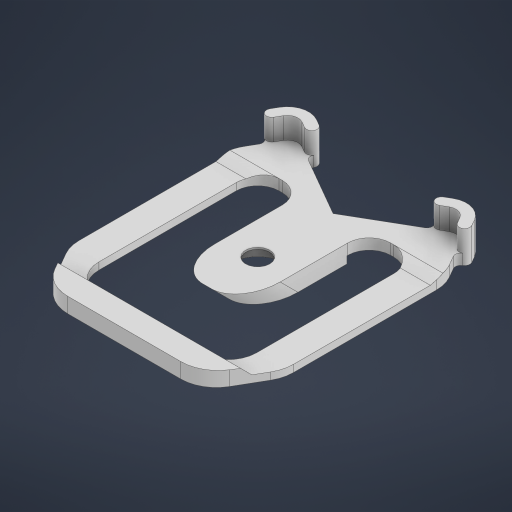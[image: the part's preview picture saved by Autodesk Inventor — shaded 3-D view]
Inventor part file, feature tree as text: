
AUTODESK INVENTOR PART (.ipt)
format: ipt  version: 2023 (Build 270158000, 158)  size: 441,344 bytes
history: native  units: in
note: dims shown in document units (in); Inventor stores cm internally (conversion verified against a paired STEP export)
features: extrude x7, chamfer x4, sketch x2, fillet x2, draft x1
ambient origin geometry x8: Origin, YZ Plane, XZ Plane, XY Plane, X Axis, Y Axis, Z Axis, Center Point
bodies: Solid1 (feature_tree)
feature tree (16):
  extrude  "Extrusion1"  Depth=0.1181in
  extrude  "Extrusion2"  Depth=0.1969in TaperAngle=0.0deg
  extrude  "Extrusion3"  Depth=0.0197in
  extrude  "Extrusion4"  Depth=0.1181in
  extrude  "Extrusion5"  Depth=0.315in
  chamfer  "Chamfer1"  Distance=0.2362in
  chamfer  "Chamfer2"  Distance=0.2362in
  chamfer  "Chamfer3"  Distance=0.5689in
  sketch  "Sketch2"  dims[d1=0.374in d3=120.0deg d4=60.0deg d5=0.1772in d6=2.9528in d11=0.0886in d14=60.0deg d15=0.1772in d16=0.0886in d17=1.5748in d18=0.1181in]
  fillet  "Fillet3"  Radius=0.0787in
  extrude  "Extrusion7"  Depth=0.0787in
  draft  "FaceDraft3"
  fillet  "Fillet10"  Radius=0.0787in
  chamfer  "Chamfer8"  Distance=0.0197in
  extrude  "Extrusion10"  Depth=0.0394in TaperAngle=0.0deg
  sketch  "Sketch7"  dims[d19=0.3937in d20=0.1969in d21=0.0in d22=0.2657in d24=0.1181in d25=0.315in d26=0.2362in d27=0.2362in d28=0.5689in d29=0.0787in d30=0.0787in d31=0.0787in d32=0.0197in d33=0.0in d34=0.0394in d35=0.0in d36=0.2362in d37=0.0in d38=0.0in d39=0.0in d40=0.0in d41=0.0in d42=0.0591in d43=0.2362in d44=0.0in d45=0.2756in d46=0.0492in d47=0.0in d48=0.2756in d49=0.0098in d50=45.0deg d52=0.0394in d53=0.1575in d54=75.0deg d55=0.0394in d56=0.1575in d57=75.0deg d66=0.315in d67=0.3937in d72=0.1575in d73=0.0in d74=45.0deg d105=0.315in d106=0.0787in d107=0.0787in d108=0.2405in d109=0.0787in d110=0.0in d51=0.0in d59=0.0in d60=0.0in d61=0.0in d62=0.0in d63=0.0in d64=0.0in d65=0.0in d68=0.0344in d69=0.0197in d70=0.0344in d104=0.0in]
